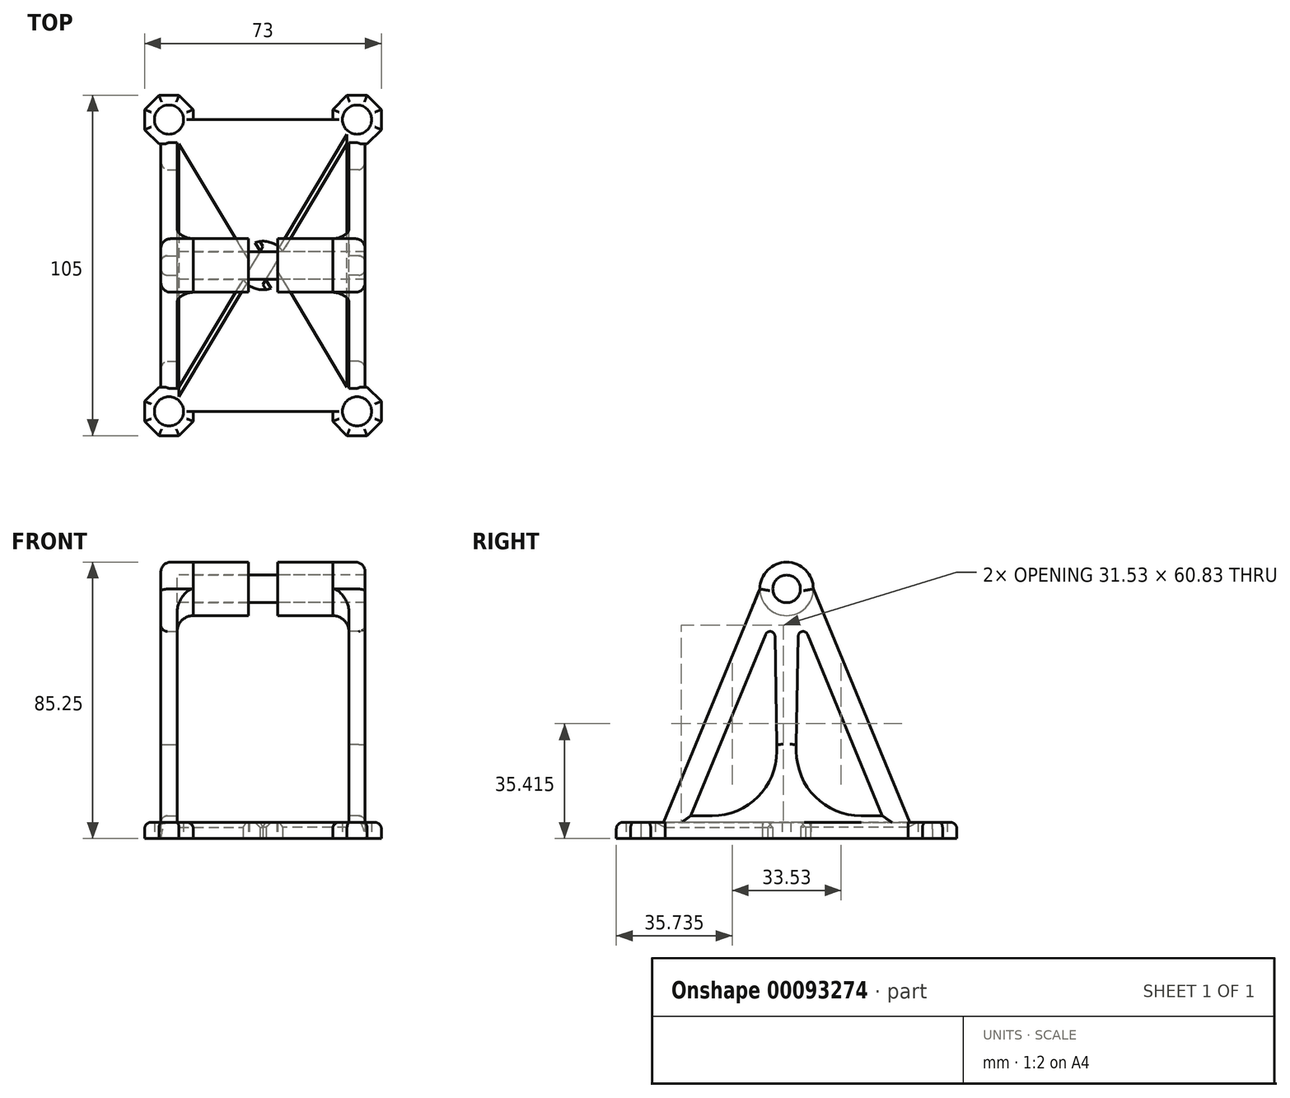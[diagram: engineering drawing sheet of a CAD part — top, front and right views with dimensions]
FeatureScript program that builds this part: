
annotation { "Feature Type Name" : "Feature", "Feature Type Description" : "" }
export const myFeature = defineFeature(function(context is Context, id is Id, definition is map)
    precondition{}
    {
        {
            assignVariable(context, id + "F0", {"name" : "shell", "anyValue" : 2.5});
        }
        {
            assignVariable(context, id + "F1", {"name" : "bucket_width", "anyValue" : 48});
        }
        {
            assignVariable(context, id + "F2", {"name" : "bearing_width", "anyValue" : 7});
        }
        {
            var Q0;
            Q0=qCreatedBy(makeId("Top.planeOp"),FACE);
            var sketch = newSketch(context, id + "F3", { "sketchPlane" : qUnion([Q0])});
            skLineSegment(sketch, "E0.bottom", {"start": v(29, -45) * mm, "end": v(-29, -45) * mm});
            skLineSegment(sketch, "E0.top", {"start": v(29, 45) * mm, "end": v(-29, 45) * mm});
            skLineSegment(sketch, "E0.left", {"start": v(29, -45) * mm, "end": v(29, 45) * mm});
            skLineSegment(sketch, "E0.right", {"start": v(-29, -45) * mm, "end": v(-29, 45) * mm});
            skPoint(sketch, "E0.middle", {"position": v(0, 0) * mm});
            skCircle(sketch, "E1.cCircle", {"center": v(-29, 45) * mm, "radius": 7.5 * mm, "construction": true});
            skLineSegment(sketch, "E1.0", {"start": v(-21.5, 48.1) * mm, "end": v(-21.5, 41.9) * mm});
            skLineSegment(sketch, "E1.1", {"start": v(-21.5, 41.9) * mm, "end": v(-25.9, 37.5) * mm});
            skLineSegment(sketch, "E1.2", {"start": v(-25.9, 37.5) * mm, "end": v(-32.1, 37.5) * mm});
            skLineSegment(sketch, "E1.3", {"start": v(-32.1, 37.5) * mm, "end": v(-36.5, 41.9) * mm});
            skLineSegment(sketch, "E1.4", {"start": v(-36.5, 41.9) * mm, "end": v(-36.5, 48.1) * mm});
            skLineSegment(sketch, "E1.5", {"start": v(-36.5, 48.1) * mm, "end": v(-32.1, 52.5) * mm});
            skLineSegment(sketch, "E1.6", {"start": v(-32.1, 52.5) * mm, "end": v(-25.9, 52.5) * mm});
            skLineSegment(sketch, "E1.7", {"start": v(-25.9, 52.5) * mm, "end": v(-21.5, 48.1) * mm});
            skPoint(sketch, "E1.0.midPoint", {"position": v(-21.5, 45) * mm});
            skCircle(sketch, "E2.cCircle", {"center": v(-29, -45) * mm, "radius": 7.5 * mm, "construction": true});
            skLineSegment(sketch, "E2.0", {"start": v(-32.1, -37.5) * mm, "end": v(-25.9, -37.5) * mm});
            skLineSegment(sketch, "E2.1", {"start": v(-25.9, -37.5) * mm, "end": v(-21.5, -41.9) * mm});
            skLineSegment(sketch, "E2.2", {"start": v(-21.5, -41.9) * mm, "end": v(-21.5, -48.1) * mm});
            skLineSegment(sketch, "E2.3", {"start": v(-21.5, -48.1) * mm, "end": v(-25.9, -52.5) * mm});
            skLineSegment(sketch, "E2.4", {"start": v(-25.9, -52.5) * mm, "end": v(-32.1, -52.5) * mm});
            skLineSegment(sketch, "E2.5", {"start": v(-32.1, -52.5) * mm, "end": v(-36.5, -48.1) * mm});
            skLineSegment(sketch, "E2.6", {"start": v(-36.5, -48.1) * mm, "end": v(-36.5, -41.9) * mm});
            skLineSegment(sketch, "E2.7", {"start": v(-36.5, -41.9) * mm, "end": v(-32.1, -37.5) * mm});
            skPoint(sketch, "E2.0.midPoint", {"position": v(-29, -37.5) * mm});
            skCircle(sketch, "E3.cCircle", {"center": v(29, -45) * mm, "radius": 7.5 * mm, "construction": true});
            skLineSegment(sketch, "E3.0", {"start": v(25.9, -37.5) * mm, "end": v(32.1, -37.5) * mm});
            skLineSegment(sketch, "E3.1", {"start": v(32.1, -37.5) * mm, "end": v(36.5, -41.9) * mm});
            skLineSegment(sketch, "E3.2", {"start": v(36.5, -41.9) * mm, "end": v(36.5, -48.1) * mm});
            skLineSegment(sketch, "E3.3", {"start": v(36.5, -48.1) * mm, "end": v(32.1, -52.5) * mm});
            skLineSegment(sketch, "E3.4", {"start": v(32.1, -52.5) * mm, "end": v(25.9, -52.5) * mm});
            skLineSegment(sketch, "E3.5", {"start": v(25.9, -52.5) * mm, "end": v(21.5, -48.1) * mm});
            skLineSegment(sketch, "E3.6", {"start": v(21.5, -48.1) * mm, "end": v(21.5, -41.9) * mm});
            skLineSegment(sketch, "E3.7", {"start": v(21.5, -41.9) * mm, "end": v(25.9, -37.5) * mm});
            skPoint(sketch, "E3.0.midPoint", {"position": v(29, -37.5) * mm});
            skCircle(sketch, "E4.cCircle", {"center": v(29, 45) * mm, "radius": 7.5 * mm, "construction": true});
            skLineSegment(sketch, "E4.0", {"start": v(32.1, 37.5) * mm, "end": v(25.9, 37.5) * mm});
            skLineSegment(sketch, "E4.1", {"start": v(25.9, 37.5) * mm, "end": v(21.5, 41.9) * mm});
            skLineSegment(sketch, "E4.2", {"start": v(21.5, 41.9) * mm, "end": v(21.5, 48.1) * mm});
            skLineSegment(sketch, "E4.3", {"start": v(21.5, 48.1) * mm, "end": v(25.9, 52.5) * mm});
            skLineSegment(sketch, "E4.4", {"start": v(25.9, 52.5) * mm, "end": v(32.1, 52.5) * mm});
            skLineSegment(sketch, "E4.5", {"start": v(32.1, 52.5) * mm, "end": v(36.5, 48.1) * mm});
            skLineSegment(sketch, "E4.6", {"start": v(36.5, 48.1) * mm, "end": v(36.5, 41.9) * mm});
            skLineSegment(sketch, "E4.7", {"start": v(36.5, 41.9) * mm, "end": v(32.1, 37.5) * mm});
            skPoint(sketch, "E4.0.midPoint", {"position": v(29, 37.5) * mm});
            skLineSegment(sketch, "E5", {"start": v(-25.9, 37.5) * mm, "end": v(21.5, -41.9) * mm});
            skLineSegment(sketch, "E6", {"start": v(25.9, -37.5) * mm, "end": v(-21.5, 41.9) * mm});
            skLineSegment(sketch, "E7", {"start": v(21.5, 41.9) * mm, "end": v(-25.9, -37.5) * mm});
            skLineSegment(sketch, "E8", {"start": v(-21.5, -41.9) * mm, "end": v(25.9, 37.5) * mm});
            skLineSegment(sketch, "E9", {"start": v(25.9, -37.5) * mm, "end": v(25.9, 37.5) * mm});
            skLineSegment(sketch, "E10", {"start": v(21.5, 41.9) * mm, "end": v(-21.5, 41.9) * mm});
            skLineSegment(sketch, "E11", {"start": v(-25.9, 37.5) * mm, "end": v(-25.9, -37.5) * mm});
            skLineSegment(sketch, "E12", {"start": v(-21.5, -41.9) * mm, "end": v(21.5, -41.9) * mm});
            skCircle(sketch, "E13", {"center": v(0, 0) * mm, "radius": 7.5 * mm});
            skCircle(sketch, "E14", {"center": v(0, 0) * mm, "radius": 4.5 * mm});
            skCircle(sketch, "E15", {"center": v(-29, 45) * mm, "radius": 4.5 * mm});
            skCircle(sketch, "E16", {"center": v(29, 45) * mm, "radius": 4.5 * mm});
            skCircle(sketch, "E17", {"center": v(29, -45) * mm, "radius": 4.5 * mm});
            skCircle(sketch, "E18", {"center": v(-29, -45) * mm, "radius": 4.5 * mm});
            skLineSegment(sketch, "E19", {"start": v(0, 0) * mm, "end": v(24, 0) * mm, "construction": true});
            skPoint(sketch, "E19.endSnap0", {"position": v(25.9, 0) * mm});
            skSolve(sketch);
        }
        {
            var Q0;
            Q0=qCreatedBy(makeId("Right.planeOp"),FACE);
            var sketch = newSketch(context, id + "F4", { "sketchPlane" : qUnion([Q0])});
            skLineSegment(sketch, "E20", {"start": v(0, 0) * mm, "end": v(0, 77) * mm, "construction": true});
            skCircle(sketch, "E21", {"center": v(0, 77) * mm, "radius": 4.25 * mm});
            skCircle(sketch, "E22.0", {"center": v(0, 77) * mm, "radius": 8.25 * mm});
            skLineSegment(sketch, "E23", {"start": v(0, 0) * mm, "end": v(40, 0) * mm});
            skLineSegment(sketch, "E24", {"start": v(0, 0) * mm, "end": v(-40, 0) * mm});
            skLineSegment(sketch, "E25", {"start": v(8.25, 77) * mm, "end": v(-8.25, 77) * mm, "construction": true});
            skLineSegment(sketch, "E26", {"start": v(8.25, 77) * mm, "end": v(40, 0) * mm});
            skLineSegment(sketch, "E27", {"start": v(-8.25, 77) * mm, "end": v(-40, 0) * mm});
            skLineSegment(sketch, "E28.0", {"start": v(3.72, 69.63) * mm, "end": v(29.54, 7) * mm});
            skLineSegment(sketch, "E28.1", {"start": v(0, 7) * mm, "end": v(29.54, 7) * mm});
            skLineSegment(sketch, "E28.2", {"start": v(0, 7) * mm, "end": v(-29.54, 7) * mm});
            skLineSegment(sketch, "E28.3", {"start": v(-3.72, 69.63) * mm, "end": v(-29.54, 7) * mm});
            skLineSegment(sketch, "E29", {"start": v(-3, 8.14) * mm, "end": v(0, 8.14) * mm, "construction": true});
            skLineSegment(sketch, "E30", {"start": v(0, 8.14) * mm, "end": v(3, 8.14) * mm, "construction": true});
            skLineSegment(sketch, "E31", {"start": v(3, 7) * mm, "end": v(3, 29.03) * mm});
            skLineSegment(sketch, "E32", {"start": v(-3, 7) * mm, "end": v(-3, 29.03) * mm});
            skLineSegment(sketch, "E33", {"start": v(3.72, 69.63) * mm, "end": v(3, 29.03) * mm});
            skLineSegment(sketch, "E34", {"start": v(-3.72, 69.63) * mm, "end": v(-3, 29.03) * mm});
            skSolve(sketch);
        }
        {
            var Q0;
            {var subQ0=sQuery(id+"F3.wireOp",EDGE,"E2.3");Q0=makeQuery(id+"F3.imprint","IMPRINT",FACE,{"disambiguationData":[TD([[makeQuery(id+"F3.imprint","IMPRINT",EDGE,{"derivedFrom":subQ0}),-1.0]])]});}
            var Q1;
            {var subQ0=sQuery(id+"F3.wireOp",EDGE,"E2.1");Q1=makeQuery(id+"F3.imprint","IMPRINT",FACE,{"disambiguationData":[TD([[makeQuery(id+"F3.imprint","IMPRINT",EDGE,{"derivedFrom":subQ0}),-1.0]])]});}
            var Q2;
            {var subQ5=sQuery(id+"F3.wireOp",EDGE,"E11");Q2=makeQuery(id+"F3.imprint","IMPRINT",FACE,{"disambiguationData":[TD([[makeQuery(id+"F3.imprint","IMPRINT",EDGE,{"derivedFrom":subQ5}),-1.0]])]});}
            var Q3;
            {var subQ9=sQuery(id+"F3.wireOp",EDGE,"E1.3");Q3=makeQuery(id+"F3.imprint","IMPRINT",FACE,{"disambiguationData":[TD([[makeQuery(id+"F3.imprint","IMPRINT",EDGE,{"derivedFrom":subQ9}),-1.0]])]});}
            var Q4;
            {var subQ0=sQuery(id+"F3.wireOp",EDGE,"E1.1");Q4=makeQuery(id+"F3.imprint","IMPRINT",FACE,{"disambiguationData":[TD([[makeQuery(id+"F3.imprint","IMPRINT",EDGE,{"derivedFrom":subQ0}),-1.0]])]});}
            var Q5;
            {var subQ5=sQuery(id+"F3.wireOp",EDGE,"E1.1");Q5=makeQuery(id+"F3.imprint","IMPRINT",FACE,{"disambiguationData":[TD([[makeQuery(id+"F3.imprint","IMPRINT",EDGE,{"derivedFrom":subQ5}),1.0]])]});}
            var Q6;
            {var subQ5=sQuery(id+"F3.wireOp",EDGE,"E10");Q6=makeQuery(id+"F3.imprint","IMPRINT",FACE,{"disambiguationData":[TD([[makeQuery(id+"F3.imprint","IMPRINT",EDGE,{"derivedFrom":subQ5}),-1.0]])]});}
            var Q7;
            {var subQ0=sQuery(id+"F3.wireOp",EDGE,"E4.3");Q7=makeQuery(id+"F3.imprint","IMPRINT",FACE,{"disambiguationData":[TD([[makeQuery(id+"F3.imprint","IMPRINT",EDGE,{"derivedFrom":subQ0}),-1.0]])]});}
            var Q8;
            {var subQ1=sQuery(id+"F3.wireOp",EDGE,"E4.1");Q8=makeQuery(id+"F3.imprint","IMPRINT",FACE,{"disambiguationData":[TD([[makeQuery(id+"F3.imprint","IMPRINT",EDGE,{"derivedFrom":subQ1}),1.0]])]});}
            var Q9;
            {var subQ0=sQuery(id+"F3.wireOp",EDGE,"E13");var subQ1=sQuery(id+"F3.wireOp",EDGE,"E5");var subQ2=makeQuery(id+"F3.imprint","INTERSECT",VERTEX,{"disambiguationData":[OD(0.0)],"derivedFrom":[subQ1,subQ0]});Q9=makeQuery(id+"F3.imprint","IMPRINT",FACE,{"disambiguationData":[TD([[makeQuery(id+"F3.imprint","IMPRINT",EDGE,{"disambiguationData":[TD([[subQ2,-1.0]])],"derivedFrom":subQ1}),1.0]])]});}
            var Q10;
            {var subQ0=sQuery(id+"F3.wireOp",EDGE,"E13");var subQ1=sQuery(id+"F3.wireOp",EDGE,"E5");var subQ2=makeQuery(id+"F3.imprint","INTERSECT",VERTEX,{"disambiguationData":[OD(0.0)],"derivedFrom":[subQ1,subQ0]});Q10=makeQuery(id+"F3.imprint","IMPRINT",FACE,{"disambiguationData":[TD([[makeQuery(id+"F3.imprint","IMPRINT",EDGE,{"disambiguationData":[TD([[subQ2,-1.0]])],"derivedFrom":subQ1}),-1.0]])]});}
            var Q11;
            {var subQ0=sQuery(id+"F3.wireOp",EDGE,"E13");var subQ1=sQuery(id+"F3.wireOp",EDGE,"E6");var subQ2=makeQuery(id+"F3.imprint","INTERSECT",VERTEX,{"disambiguationData":[OD(0.0)],"derivedFrom":[subQ1,subQ0]});Q11=makeQuery(id+"F3.imprint","IMPRINT",FACE,{"disambiguationData":[TD([[makeQuery(id+"F3.imprint","IMPRINT",EDGE,{"disambiguationData":[TD([[subQ2,-1.0]])],"derivedFrom":subQ1}),-1.0]])]});}
            var Q12;
            {var subQ6=sQuery(id+"F3.wireOp",EDGE,"E3.7");Q12=makeQuery(id+"F3.imprint","IMPRINT",FACE,{"disambiguationData":[TD([[makeQuery(id+"F3.imprint","IMPRINT",EDGE,{"derivedFrom":subQ6}),1.0]])]});}
            var Q13;
            {var subQ1=sQuery(id+"F3.wireOp",EDGE,"E2.1");Q13=makeQuery(id+"F3.imprint","IMPRINT",FACE,{"disambiguationData":[TD([[makeQuery(id+"F3.imprint","IMPRINT",EDGE,{"derivedFrom":subQ1}),1.0]])]});}
            var Q14;
            {var subQ5=sQuery(id+"F3.wireOp",EDGE,"E12");Q14=makeQuery(id+"F3.imprint","IMPRINT",FACE,{"disambiguationData":[TD([[makeQuery(id+"F3.imprint","IMPRINT",EDGE,{"derivedFrom":subQ5}),-1.0]])]});}
            var Q15;
            {var subQ0=sQuery(id+"F3.wireOp",EDGE,"E3.7");Q15=makeQuery(id+"F3.imprint","IMPRINT",FACE,{"disambiguationData":[TD([[makeQuery(id+"F3.imprint","IMPRINT",EDGE,{"derivedFrom":subQ0}),-1.0]])]});}
            var Q16;
            {var subQ5=sQuery(id+"F3.wireOp",EDGE,"E9");Q16=makeQuery(id+"F3.imprint","IMPRINT",FACE,{"disambiguationData":[TD([[makeQuery(id+"F3.imprint","IMPRINT",EDGE,{"derivedFrom":subQ5}),-1.0]])]});}
            var Q17;
            {var subQ0=sQuery(id+"F3.wireOp",EDGE,"E3.1");Q17=makeQuery(id+"F3.imprint","IMPRINT",FACE,{"disambiguationData":[TD([[makeQuery(id+"F3.imprint","IMPRINT",EDGE,{"derivedFrom":subQ0}),-1.0]])]});}
            var Q18;
            {var subQ9=sQuery(id+"F3.wireOp",EDGE,"E4.1");Q18=makeQuery(id+"F3.imprint","IMPRINT",FACE,{"disambiguationData":[TD([[makeQuery(id+"F3.imprint","IMPRINT",EDGE,{"derivedFrom":subQ9}),-1.0]])]});}
            var Q19;
            {var subQ0=sQuery(id+"F3.wireOp",EDGE,"E14");var subQ1=sQuery(id+"F3.wireOp",EDGE,"E5");var subQ2=makeQuery(id+"F3.imprint","INTERSECT",VERTEX,{"disambiguationData":[OD(1.0)],"derivedFrom":[subQ1,subQ0]});Q19=makeQuery(id+"F3.imprint","IMPRINT",FACE,{"disambiguationData":[TD([[makeQuery(id+"F3.imprint","IMPRINT",EDGE,{"disambiguationData":[TD([[subQ2,-1.0]])],"derivedFrom":subQ1}),-1.0]])]});}
            var Q20;
            {var subQ0=sQuery(id+"F3.wireOp",EDGE,"E14");var subQ1=sQuery(id+"F3.wireOp",EDGE,"E5");var subQ2=makeQuery(id+"F3.imprint","INTERSECT",VERTEX,{"disambiguationData":[OD(1.0)],"derivedFrom":[subQ1,subQ0]});Q20=makeQuery(id+"F3.imprint","IMPRINT",FACE,{"disambiguationData":[TD([[makeQuery(id+"F3.imprint","IMPRINT",EDGE,{"disambiguationData":[TD([[subQ2,-1.0]])],"derivedFrom":subQ1}),1.0]])]});}
            var Q21;
            {var subQ0=sQuery(id+"F3.wireOp",EDGE,"E14");var subQ1=sQuery(id+"F3.wireOp",EDGE,"E6");var subQ2=makeQuery(id+"F3.imprint","INTERSECT",VERTEX,{"disambiguationData":[OD(1.0)],"derivedFrom":[subQ1,subQ0]});Q21=makeQuery(id+"F3.imprint","IMPRINT",FACE,{"disambiguationData":[TD([[makeQuery(id+"F3.imprint","IMPRINT",EDGE,{"disambiguationData":[TD([[subQ2,-1.0]])],"derivedFrom":subQ1}),-1.0]])]});}
            var Q22;
            {var subQ0=sQuery(id+"F3.wireOp",EDGE,"E14");var subQ1=sQuery(id+"F3.wireOp",EDGE,"E6");var subQ2=makeQuery(id+"F3.imprint","INTERSECT",VERTEX,{"disambiguationData":[OD(1.0)],"derivedFrom":[subQ1,subQ0]});Q22=makeQuery(id+"F3.imprint","IMPRINT",FACE,{"disambiguationData":[TD([[makeQuery(id+"F3.imprint","IMPRINT",EDGE,{"disambiguationData":[TD([[subQ2,-1.0]])],"derivedFrom":subQ1}),1.0]])]});}
            var Q23;
            {var subQ0=sQuery(id+"F3.wireOp",EDGE,"E13");var subQ1=sQuery(id+"F3.wireOp",EDGE,"E6");var subQ2=makeQuery(id+"F3.imprint","INTERSECT",VERTEX,{"disambiguationData":[OD(0.0)],"derivedFrom":[subQ1,subQ0]});Q23=makeQuery(id+"F3.imprint","IMPRINT",FACE,{"disambiguationData":[TD([[makeQuery(id+"F3.imprint","IMPRINT",EDGE,{"disambiguationData":[TD([[subQ2,-1.0]])],"derivedFrom":subQ1}),1.0]])]});}
            var Q24;
            {var subQ0=sQuery(id+"F3.wireOp",EDGE,"E13");var subQ1=sQuery(id+"F3.wireOp",EDGE,"E5");var subQ2=makeQuery(id+"F3.imprint","INTERSECT",VERTEX,{"disambiguationData":[OD(1.0)],"derivedFrom":[subQ1,subQ0]});Q24=makeQuery(id+"F3.imprint","IMPRINT",FACE,{"disambiguationData":[TD([[makeQuery(id+"F3.imprint","IMPRINT",EDGE,{"disambiguationData":[TD([[subQ2,-1.0]])],"derivedFrom":subQ1}),1.0]])]});}
            var Q25;
            {var subQ0=sQuery(id+"F3.wireOp",EDGE,"E13");var subQ1=sQuery(id+"F3.wireOp",EDGE,"E6");var subQ2=makeQuery(id+"F3.imprint","INTERSECT",VERTEX,{"disambiguationData":[OD(1.0)],"derivedFrom":[subQ1,subQ0]});Q25=makeQuery(id+"F3.imprint","IMPRINT",FACE,{"disambiguationData":[TD([[makeQuery(id+"F3.imprint","IMPRINT",EDGE,{"disambiguationData":[TD([[subQ2,-1.0]])],"derivedFrom":subQ1}),1.0]])]});}
            extrude(context, id + "F5", {"entities" : qUnion([Q0, Q1, Q2, Q3, Q4, Q5, Q6, Q7, Q8, Q9, Q10, Q11, Q12, Q13, Q14, Q15, Q16, Q17, Q18, Q19, Q20, Q21, Q22, Q23, Q24, Q25]), "depth" : 5 * mm});
        }
        {
            var Q0;
            {var subQ5=sQuery(id+"F4.wireOp",EDGE,"E27");Q0=makeQuery(id+"F4.imprint","IMPRINT",FACE,{"disambiguationData":[TD([[makeQuery(id+"F4.imprint","IMPRINT",EDGE,{"derivedFrom":subQ5}),1.0]])]});}
            var Q1;
            {var subQ4=sQuery(id+"F4.wireOp",EDGE,"E26");Q1=makeQuery(id+"F4.imprint","IMPRINT",FACE,{"disambiguationData":[TD([[makeQuery(id+"F4.imprint","IMPRINT",EDGE,{"derivedFrom":subQ4}),-1.0]])]});}
            var Q2;
            {var subQ7=sQuery(id+"F4.wireOp",EDGE,"E24");var subQ8=sQuery(id+"F4.wireOp",EDGE,"E23");var subQ9=makeQuery(id+"F4.imprint","INTERSECT",VERTEX,{"derivedFrom":[subQ8,subQ7]});Q2=makeQuery(id+"F4.imprint","IMPRINT",FACE,{"disambiguationData":[TD([[makeQuery(id+"F4.imprint","IMPRINT",EDGE,{"disambiguationData":[TD([[subQ9,-1.0]])],"derivedFrom":subQ8}),1.0]])]});}
            var Q3;
            Q3=makeQuery(id+"F4.imprint","IMPRINT",FACE,{"disambiguationData":[TD([[makeQuery(id+"F4.imprint","IMPRINT",EDGE,{"derivedFrom":sQuery(id+"F4.wireOp",EDGE,"E21")}),-1.0]])]});
            var Q4;
            Q4=makeQuery(id+"F4.imprint","IMPRINT",FACE,{"disambiguationData":[TD([[makeQuery(id+"F4.imprint","IMPRINT",EDGE,{"derivedFrom":sQuery(id+"F4.wireOp",EDGE,"E21")}),-1.0]])]});
            var Q5;
            {var subQ5=sQuery(id+"F4.wireOp",EDGE,"E27");Q5=makeQuery(id+"F4.imprint","IMPRINT",FACE,{"disambiguationData":[TD([[makeQuery(id+"F4.imprint","IMPRINT",EDGE,{"derivedFrom":subQ5}),1.0]])]});}
            var Q6;
            Q6=makeQuery(id+"F4.imprint","IMPRINT",FACE,{"disambiguationData":[TD([[makeQuery(id+"F4.imprint","IMPRINT",EDGE,{"derivedFrom":sQuery(id+"F4.wireOp",EDGE,"908c2eed-a312-402c-85c4-66b7b7d972e5.4")}),1.0]])]});
            var Q7;
            {var subQ3=sQuery(id+"F4.wireOp",EDGE,"3dacc5b1-dc25-4eaf-9f2e-9f7119090daa.0");var subQ5=sQuery(id+"F4.wireOp",EDGE,"908c2eed-a312-402c-85c4-66b7b7d972e5.0");var subQ6=makeQuery(id+"F4.imprint","INTERSECT",VERTEX,{"derivedFrom":[subQ3,subQ5]});Q7=makeQuery(id+"F4.imprint","IMPRINT",FACE,{"disambiguationData":[TD([[makeQuery(id+"F4.imprint","IMPRINT",EDGE,{"disambiguationData":[TD([[subQ6,1.0]])],"derivedFrom":subQ3}),1.0]])]});}
            var Q8;
            Q8=makeQuery(id+"F4.imprint","IMPRINT",FACE,{"disambiguationData":[TD([[makeQuery(id+"F4.imprint","IMPRINT",EDGE,{"derivedFrom":sQuery(id+"F4.wireOp",EDGE,"908c2eed-a312-402c-85c4-66b7b7d972e5.1")}),1.0]])]});
            var Q9;
            {var subQ1=sQuery(id+"F4.wireOp",EDGE,"E28.2");var subQ6=sQuery(id+"F4.wireOp",EDGE,"E28.1");var subQ10=makeQuery(id+"F4.imprint","INTERSECT",VERTEX,{"derivedFrom":[subQ6,subQ1]});Q9=makeQuery(id+"F4.imprint","IMPRINT",FACE,{"disambiguationData":[TD([[makeQuery(id+"F4.imprint","IMPRINT",EDGE,{"disambiguationData":[TD([[subQ10,-1.0]])],"derivedFrom":subQ6}),1.0]])]});}
            var Q10;
            {var subQ4=sQuery(id+"F4.wireOp",EDGE,"E26");Q10=makeQuery(id+"F4.imprint","IMPRINT",FACE,{"disambiguationData":[TD([[makeQuery(id+"F4.imprint","IMPRINT",EDGE,{"derivedFrom":subQ4}),-1.0]])]});}
            var Q11;
            {var subQ0=sQuery(id+"F4.wireOp",EDGE,"908c2eed-a312-402c-85c4-66b7b7d972e5.1");Q11=makeQuery(id+"F4.imprint","IMPRINT",FACE,{"disambiguationData":[TD([[makeQuery(id+"F4.imprint","IMPRINT",EDGE,{"derivedFrom":subQ0}),-1.0]])]});}
            var Q12;
            {var subQ1=sQuery(id+"F4.wireOp",EDGE,"908c2eed-a312-402c-85c4-66b7b7d972e5.2");var subQ3=sQuery(id+"F4.wireOp",EDGE,"3dacc5b1-dc25-4eaf-9f2e-9f7119090daa.0");var subQ4=makeQuery(id+"F4.imprint","INTERSECT",VERTEX,{"derivedFrom":[subQ3,subQ1]});Q12=makeQuery(id+"F4.imprint","IMPRINT",FACE,{"disambiguationData":[TD([[makeQuery(id+"F4.imprint","IMPRINT",EDGE,{"disambiguationData":[TD([[subQ4,-1.0]])],"derivedFrom":subQ3}),1.0]])]});}
            var Q13;
            {var subQ0=sQuery(id+"F4.wireOp",EDGE,"908c2eed-a312-402c-85c4-66b7b7d972e5.4");Q13=makeQuery(id+"F4.imprint","IMPRINT",FACE,{"disambiguationData":[TD([[makeQuery(id+"F4.imprint","IMPRINT",EDGE,{"derivedFrom":subQ0}),-1.0]])]});}
            extrude(context, id + "F6", {"entities" : qUnion([Q0, Q1, Q2, Q3, Q4, Q5, Q6, Q7, Q8, Q9, Q10, Q11, Q12, Q13]), "operationType" : NewBodyOperationType.ADD, "depth" : (getVariable(context, 'bucket_width') / 2 + getVariable(context, 'shell') * 3) * mm, "hasSecondDirection" : true, "secondDirectionOppositeDirection" : false, "secondDirectionDepth" : (getVariable(context, 'bucket_width') / 2 + getVariable(context, 'shell')) * mm});
        }
        {
            var Q0;
            {var subQ5=sQuery(id+"F4.wireOp",EDGE,"E27");Q0=makeQuery(id+"F4.imprint","IMPRINT",FACE,{"disambiguationData":[TD([[makeQuery(id+"F4.imprint","IMPRINT",EDGE,{"derivedFrom":subQ5}),1.0]])]});}
            var Q1;
            {var subQ4=sQuery(id+"F4.wireOp",EDGE,"E26");Q1=makeQuery(id+"F4.imprint","IMPRINT",FACE,{"disambiguationData":[TD([[makeQuery(id+"F4.imprint","IMPRINT",EDGE,{"derivedFrom":subQ4}),-1.0]])]});}
            var Q2;
            {var subQ7=sQuery(id+"F4.wireOp",EDGE,"E24");var subQ8=sQuery(id+"F4.wireOp",EDGE,"E23");var subQ9=makeQuery(id+"F4.imprint","INTERSECT",VERTEX,{"derivedFrom":[subQ8,subQ7]});Q2=makeQuery(id+"F4.imprint","IMPRINT",FACE,{"disambiguationData":[TD([[makeQuery(id+"F4.imprint","IMPRINT",EDGE,{"disambiguationData":[TD([[subQ9,-1.0]])],"derivedFrom":subQ8}),1.0]])]});}
            var Q3;
            Q3=makeQuery(id+"F4.imprint","IMPRINT",FACE,{"disambiguationData":[TD([[makeQuery(id+"F4.imprint","IMPRINT",EDGE,{"derivedFrom":sQuery(id+"F4.wireOp",EDGE,"E21")}),-1.0]])]});
            var Q4;
            Q4=makeQuery(id+"F4.imprint","IMPRINT",FACE,{"disambiguationData":[TD([[makeQuery(id+"F4.imprint","IMPRINT",EDGE,{"derivedFrom":sQuery(id+"F4.wireOp",EDGE,"E21")}),1.0]])]});
            var Q5;
            Q5=makeQuery(id+"F4.imprint","IMPRINT",FACE,{"disambiguationData":[TD([[makeQuery(id+"F4.imprint","IMPRINT",EDGE,{"derivedFrom":sQuery(id+"F4.wireOp",EDGE,"E21")}),-1.0]])]});
            var Q6;
            Q6=makeQuery(id+"F4.imprint","IMPRINT",FACE,{"disambiguationData":[TD([[makeQuery(id+"F4.imprint","IMPRINT",EDGE,{"derivedFrom":sQuery(id+"F4.wireOp",EDGE,"E21")}),-1.0]])]});
            var Q7;
            Q7=makeQuery(id+"F4.imprint","IMPRINT",FACE,{"disambiguationData":[TD([[makeQuery(id+"F4.imprint","IMPRINT",EDGE,{"derivedFrom":sQuery(id+"F4.wireOp",EDGE,"E21")}),-1.0]])]});
            var Q8;
            {var subQ5=sQuery(id+"F4.wireOp",EDGE,"E27");Q8=makeQuery(id+"F4.imprint","IMPRINT",FACE,{"disambiguationData":[TD([[makeQuery(id+"F4.imprint","IMPRINT",EDGE,{"derivedFrom":subQ5}),1.0]])]});}
            var Q9;
            {var subQ4=sQuery(id+"F4.wireOp",EDGE,"E26");Q9=makeQuery(id+"F4.imprint","IMPRINT",FACE,{"disambiguationData":[TD([[makeQuery(id+"F4.imprint","IMPRINT",EDGE,{"derivedFrom":subQ4}),-1.0]])]});}
            var Q10;
            Q10=makeQuery(id+"F4.imprint","IMPRINT",FACE,{"disambiguationData":[TD([[makeQuery(id+"F4.imprint","IMPRINT",EDGE,{"derivedFrom":sQuery(id+"F4.wireOp",EDGE,"908c2eed-a312-402c-85c4-66b7b7d972e5.1")}),1.0]])]});
            var Q11;
            {var subQ5=sQuery(id+"F4.wireOp",EDGE,"908c2eed-a312-402c-85c4-66b7b7d972e5.1");Q11=makeQuery(id+"F4.imprint","IMPRINT",FACE,{"disambiguationData":[TD([[makeQuery(id+"F4.imprint","IMPRINT",EDGE,{"derivedFrom":subQ5}),-1.0]])]});}
            var Q12;
            {var subQ3=sQuery(id+"F4.wireOp",EDGE,"3dacc5b1-dc25-4eaf-9f2e-9f7119090daa.0");var subQ5=sQuery(id+"F4.wireOp",EDGE,"908c2eed-a312-402c-85c4-66b7b7d972e5.0");var subQ6=makeQuery(id+"F4.imprint","INTERSECT",VERTEX,{"derivedFrom":[subQ3,subQ5]});Q12=makeQuery(id+"F4.imprint","IMPRINT",FACE,{"disambiguationData":[TD([[makeQuery(id+"F4.imprint","IMPRINT",EDGE,{"disambiguationData":[TD([[subQ6,1.0]])],"derivedFrom":subQ3}),1.0]])]});}
            var Q13;
            {var subQ5=sQuery(id+"F4.wireOp",EDGE,"908c2eed-a312-402c-85c4-66b7b7d972e5.4");Q13=makeQuery(id+"F4.imprint","IMPRINT",FACE,{"disambiguationData":[TD([[makeQuery(id+"F4.imprint","IMPRINT",EDGE,{"derivedFrom":subQ5}),-1.0]])]});}
            var Q14;
            Q14=makeQuery(id+"F4.imprint","IMPRINT",FACE,{"disambiguationData":[TD([[makeQuery(id+"F4.imprint","IMPRINT",EDGE,{"derivedFrom":sQuery(id+"F4.wireOp",EDGE,"908c2eed-a312-402c-85c4-66b7b7d972e5.4")}),1.0]])]});
            var Q15;
            {var subQ1=sQuery(id+"F4.wireOp",EDGE,"E28.2");var subQ6=sQuery(id+"F4.wireOp",EDGE,"E28.1");var subQ10=makeQuery(id+"F4.imprint","INTERSECT",VERTEX,{"derivedFrom":[subQ6,subQ1]});Q15=makeQuery(id+"F4.imprint","IMPRINT",FACE,{"disambiguationData":[TD([[makeQuery(id+"F4.imprint","IMPRINT",EDGE,{"disambiguationData":[TD([[subQ10,-1.0]])],"derivedFrom":subQ6}),1.0]])]});}
            var Q16;
            {var subQ1=sQuery(id+"F4.wireOp",EDGE,"908c2eed-a312-402c-85c4-66b7b7d972e5.2");var subQ3=sQuery(id+"F4.wireOp",EDGE,"3dacc5b1-dc25-4eaf-9f2e-9f7119090daa.0");var subQ4=makeQuery(id+"F4.imprint","INTERSECT",VERTEX,{"derivedFrom":[subQ3,subQ1]});Q16=makeQuery(id+"F4.imprint","IMPRINT",FACE,{"disambiguationData":[TD([[makeQuery(id+"F4.imprint","IMPRINT",EDGE,{"disambiguationData":[TD([[subQ4,-1.0]])],"derivedFrom":subQ3}),1.0]])]});}
            extrude(context, id + "F7", {"entities" : qUnion([Q0, Q1, Q2, Q3, Q4, Q5, Q6, Q7, Q8, Q9, Q10, Q11, Q12, Q13, Q14, Q15, Q16]), "operationType" : NewBodyOperationType.ADD, "oppositeDirection" : true, "depth" : (getVariable(context, 'bucket_width') / 2 + getVariable(context, 'shell') * 3) * mm, "hasSecondDirection" : true, "secondDirectionOppositeDirection" : true, "secondDirectionDepth" : (getVariable(context, 'bucket_width') / 2 + getVariable(context, 'shell')) * mm});
        }
        {
            var Q0;
            Q0=makeQuery(id+"F4.imprint","IMPRINT",FACE,{"disambiguationData":[TD([[makeQuery(id+"F4.imprint","IMPRINT",EDGE,{"derivedFrom":sQuery(id+"F4.wireOp",EDGE,"E21")}),-1.0]])]});
            var Q1;
            {var subQ2=sQuery(id+"F4.wireOp",EDGE,"E28.0");var subQ7=sQuery(id+"F4.wireOp",EDGE,"E21");var subQ9=makeQuery(id+"F4.imprint","INTERSECT",VERTEX,{"derivedFrom":[subQ7,subQ2]});Q1=makeQuery(id+"F4.imprint","IMPRINT",FACE,{"disambiguationData":[TD([[makeQuery(id+"F4.imprint","IMPRINT",EDGE,{"disambiguationData":[TD([[subQ9,-1.0]])],"derivedFrom":subQ7}),-1.0]])]});}
            extrude(context, id + "F8", {"entities" : qUnion([Q0, Q1]), "operationType" : NewBodyOperationType.ADD, "depth" : (getVariable(context, 'bucket_width') / 2 + 7) * mm, "hasSecondDirection" : true, "secondDirectionOppositeDirection" : false, "secondDirectionDepth" : (getVariable(context, 'bucket_width') / 2 - getVariable(context, 'shell')) * mm});
        }
        {
            var Q0;
            {var subQ2=sQuery(id+"F4.wireOp",EDGE,"E28.3");var subQ7=sQuery(id+"F4.wireOp",EDGE,"E21");var subQ9=makeQuery(id+"F4.imprint","INTERSECT",VERTEX,{"derivedFrom":[subQ7,subQ2]});Q0=makeQuery(id+"F4.imprint","IMPRINT",FACE,{"disambiguationData":[TD([[makeQuery(id+"F4.imprint","IMPRINT",EDGE,{"disambiguationData":[TD([[subQ9,1.0]])],"derivedFrom":subQ7}),-1.0]])]});}
            var Q1;
            {var subQ0=sQuery(id+"F4.wireOp",EDGE,"dfa7258b-916b-41aa-b35c-9c5d3d2d38c0.0");var subQ1=sQuery(id+"F4.wireOp",EDGE,"E21");var subQ2=makeQuery(id+"F4.imprint","INTERSECT",VERTEX,{"derivedFrom":[subQ1,subQ0]});Q1=makeQuery(id+"F4.imprint","IMPRINT",FACE,{"disambiguationData":[TD([[makeQuery(id+"F4.imprint","IMPRINT",EDGE,{"disambiguationData":[TD([[subQ2,-1.0]])],"derivedFrom":subQ1}),-1.0]])]});}
            var Q2;
            {var subQ0=sQuery(id+"F4.wireOp",EDGE,"3dacc5b1-dc25-4eaf-9f2e-9f7119090daa.0");var subQ1=sQuery(id+"F4.wireOp",EDGE,"E21");var subQ2=makeQuery(id+"F4.imprint","INTERSECT",VERTEX,{"derivedFrom":[subQ1,subQ0]});Q2=makeQuery(id+"F4.imprint","IMPRINT",FACE,{"disambiguationData":[TD([[makeQuery(id+"F4.imprint","IMPRINT",EDGE,{"disambiguationData":[TD([[subQ2,-1.0]])],"derivedFrom":subQ1}),-1.0]])]});}
            var Q3;
            {var subQ0=sQuery(id+"F4.wireOp",EDGE,"dfa7258b-916b-41aa-b35c-9c5d3d2d38c0.0");var subQ1=sQuery(id+"F4.wireOp",EDGE,"E21");var subQ2=makeQuery(id+"F4.imprint","INTERSECT",VERTEX,{"derivedFrom":[subQ1,subQ0]});Q3=makeQuery(id+"F4.imprint","IMPRINT",FACE,{"disambiguationData":[TD([[makeQuery(id+"F4.imprint","IMPRINT",EDGE,{"disambiguationData":[TD([[subQ2,1.0]])],"derivedFrom":subQ1}),-1.0]])]});}
            var Q4;
            {var subQ0=sQuery(id+"F4.wireOp",EDGE,"E21");var subQ1=makeQuery(id+"F4.imprint","INTERSECT",VERTEX,{"derivedFrom":[subQ0,sQuery(id+"F4.wireOp",EDGE,"dfa7258b-916b-41aa-b35c-9c5d3d2d38c0.0")]});Q4=makeQuery(id+"F4.imprint","IMPRINT",FACE,{"disambiguationData":[TD([[makeQuery(id+"F4.imprint","IMPRINT",EDGE,{"disambiguationData":[TD([[subQ1,1.0]])],"derivedFrom":subQ0}),1.0]])]});}
            extrude(context, id + "F9", {"entities" : qUnion([Q0, Q1, Q2, Q3, Q4]), "operationType" : NewBodyOperationType.ADD, "oppositeDirection" : true, "depth" : (getVariable(context, 'bucket_width') / 2 + 7) * mm, "hasSecondDirection" : true, "secondDirectionOppositeDirection" : true, "secondDirectionDepth" : ((getVariable(context, 'bucket_width') / 2) - getVariable(context, 'shell')) * mm});
        }
        {
            var Q0;
            {var subQ0=sQuery(id+"F3.wireOp",EDGE,"E0.right");var subQ1=sQuery(id+"F3.wireOp",EDGE,"E0.bottom");var subQ2=makeQuery(id+"F3.imprint","INTERSECT",VERTEX,{"derivedFrom":[subQ1,subQ0]});Q0=makeQuery(id+"F3.imprint","IMPRINT",FACE,{"disambiguationData":[TD([[makeQuery(id+"F3.imprint","IMPRINT",EDGE,{"disambiguationData":[TD([[subQ2,1.0]])],"derivedFrom":subQ1}),-1.0]])]});}
            var Q1;
            {var subQ0=sQuery(id+"F3.wireOp",EDGE,"E0.right");var subQ1=sQuery(id+"F3.wireOp",EDGE,"E0.bottom");var subQ2=makeQuery(id+"F3.imprint","INTERSECT",VERTEX,{"derivedFrom":[subQ1,subQ0]});Q1=makeQuery(id+"F3.imprint","IMPRINT",FACE,{"disambiguationData":[TD([[makeQuery(id+"F3.imprint","IMPRINT",EDGE,{"disambiguationData":[TD([[subQ2,1.0]])],"derivedFrom":subQ1}),1.0]])]});}
            var Q2;
            {var subQ0=sQuery(id+"F3.wireOp",EDGE,"E0.left");var subQ1=sQuery(id+"F3.wireOp",EDGE,"E0.bottom");var subQ2=makeQuery(id+"F3.imprint","INTERSECT",VERTEX,{"derivedFrom":[subQ1,subQ0]});Q2=makeQuery(id+"F3.imprint","IMPRINT",FACE,{"disambiguationData":[TD([[makeQuery(id+"F3.imprint","IMPRINT",EDGE,{"disambiguationData":[TD([[subQ2,-1.0]])],"derivedFrom":subQ1}),1.0]])]});}
            var Q3;
            {var subQ0=sQuery(id+"F3.wireOp",EDGE,"E0.left");var subQ1=sQuery(id+"F3.wireOp",EDGE,"E0.bottom");var subQ2=makeQuery(id+"F3.imprint","INTERSECT",VERTEX,{"derivedFrom":[subQ1,subQ0]});Q3=makeQuery(id+"F3.imprint","IMPRINT",FACE,{"disambiguationData":[TD([[makeQuery(id+"F3.imprint","IMPRINT",EDGE,{"disambiguationData":[TD([[subQ2,-1.0]])],"derivedFrom":subQ1}),-1.0]])]});}
            var Q4;
            {var subQ0=sQuery(id+"F3.wireOp",EDGE,"E0.left");var subQ1=sQuery(id+"F3.wireOp",EDGE,"E0.top");var subQ2=makeQuery(id+"F3.imprint","INTERSECT",VERTEX,{"derivedFrom":[subQ1,subQ0]});Q4=makeQuery(id+"F3.imprint","IMPRINT",FACE,{"disambiguationData":[TD([[makeQuery(id+"F3.imprint","IMPRINT",EDGE,{"disambiguationData":[TD([[subQ2,-1.0]])],"derivedFrom":subQ1}),1.0]])]});}
            var Q5;
            {var subQ0=sQuery(id+"F3.wireOp",EDGE,"E0.left");var subQ1=sQuery(id+"F3.wireOp",EDGE,"E0.top");var subQ2=makeQuery(id+"F3.imprint","INTERSECT",VERTEX,{"derivedFrom":[subQ1,subQ0]});Q5=makeQuery(id+"F3.imprint","IMPRINT",FACE,{"disambiguationData":[TD([[makeQuery(id+"F3.imprint","IMPRINT",EDGE,{"disambiguationData":[TD([[subQ2,-1.0]])],"derivedFrom":subQ1}),-1.0]])]});}
            var Q6;
            {var subQ0=sQuery(id+"F3.wireOp",EDGE,"E0.right");var subQ1=sQuery(id+"F3.wireOp",EDGE,"E0.top");var subQ2=makeQuery(id+"F3.imprint","INTERSECT",VERTEX,{"derivedFrom":[subQ1,subQ0]});Q6=makeQuery(id+"F3.imprint","IMPRINT",FACE,{"disambiguationData":[TD([[makeQuery(id+"F3.imprint","IMPRINT",EDGE,{"disambiguationData":[TD([[subQ2,1.0]])],"derivedFrom":subQ1}),1.0]])]});}
            var Q7;
            {var subQ0=sQuery(id+"F3.wireOp",EDGE,"E0.right");var subQ1=sQuery(id+"F3.wireOp",EDGE,"E0.top");var subQ2=makeQuery(id+"F3.imprint","INTERSECT",VERTEX,{"derivedFrom":[subQ1,subQ0]});Q7=makeQuery(id+"F3.imprint","IMPRINT",FACE,{"disambiguationData":[TD([[makeQuery(id+"F3.imprint","IMPRINT",EDGE,{"disambiguationData":[TD([[subQ2,1.0]])],"derivedFrom":subQ1}),-1.0]])]});}
            extrude(context, id + "F10", {"entities" : qUnion([Q0, Q1, Q2, Q3, Q4, Q5, Q6, Q7]), "operationType" : NewBodyOperationType.REMOVE, "oppositeDirection" : true, "depth" : 25 * mm, "hasSecondDirection" : true, "secondDirectionOppositeDirection" : false, "secondDirectionDepth" : 25 * mm});
        }
        {
            var Q0;
            Q0=makeQuery(id+"F6.opExtrude","SWEPT_EDGE",EDGE,{"disambiguationData":[OSD([sQuery(id+"F4.wireOp",EDGE,"E22.0"),sQuery(id+"F4.wireOp",EDGE,"E28.3"),sQuery(id+"F4.wireOp",EDGE,"E34")])]});
            var Q1;
            Q1=makeQuery(id+"F6.opExtrude","SWEPT_EDGE",EDGE,{"disambiguationData":[OSD([sQuery(id+"F4.wireOp",EDGE,"E22.0"),sQuery(id+"F4.wireOp",EDGE,"E28.0"),sQuery(id+"F4.wireOp",EDGE,"E33")])]});
            var Q2;
            Q2=makeQuery(id+"F7.opExtrude","SWEPT_EDGE",EDGE,{"disambiguationData":[OSD([sQuery(id+"F4.wireOp",EDGE,"E22.0"),sQuery(id+"F4.wireOp",EDGE,"E28.0"),sQuery(id+"F4.wireOp",EDGE,"E33")])]});
            var Q3;
            Q3=makeQuery(id+"F7.opExtrude","SWEPT_EDGE",EDGE,{"disambiguationData":[OSD([sQuery(id+"F4.wireOp",EDGE,"E22.0"),sQuery(id+"F4.wireOp",EDGE,"E28.3"),sQuery(id+"F4.wireOp",EDGE,"E34")])]});
            fillet(context, id + "F11", {"entities" : qUnion([Q0, Q1, Q2, Q3]), "radius" : 1.5 * mm, "tangentPropagation" : true, "allowEdgeOverflow" : false});
        }
        {
            var Q0;
            Q0=makeQuery(id+"F6.opExtrude","SWEPT_EDGE",EDGE,{"disambiguationData":[OSD([sQuery(id+"F4.wireOp",EDGE,"E28.1"),sQuery(id+"F4.wireOp",EDGE,"E31")])]});
            var Q1;
            Q1=makeQuery(id+"F6.opExtrude","SWEPT_EDGE",EDGE,{"disambiguationData":[OSD([sQuery(id+"F4.wireOp",EDGE,"E28.2"),sQuery(id+"F4.wireOp",EDGE,"E32")])]});
            var Q2;
            Q2=makeQuery(id+"F7.opExtrude","SWEPT_EDGE",EDGE,{"disambiguationData":[OSD([sQuery(id+"F4.wireOp",EDGE,"E28.2"),sQuery(id+"F4.wireOp",EDGE,"E32")])]});
            var Q3;
            Q3=makeQuery(id+"F7.opExtrude","SWEPT_EDGE",EDGE,{"disambiguationData":[OSD([sQuery(id+"F4.wireOp",EDGE,"E28.1"),sQuery(id+"F4.wireOp",EDGE,"E31")])]});
            fillet(context, id + "F12", {"entities" : qUnion([Q0, Q1, Q2, Q3]), "radius" : 20 * mm, "tangentPropagation" : true, "allowEdgeOverflow" : false});
        }
        {
            var Q0;
            Q0=makeQuery(id+"F5.opExtrude","CAP_EDGE",EDGE,{"disambiguationData":[OSD([sQuery(id+"F3.wireOp",EDGE,"E2.4")])],"isStart":false});
            var Q1;
            Q1=makeQuery(id+"F5.opExtrude","CAP_EDGE",EDGE,{"disambiguationData":[OSD([sQuery(id+"F3.wireOp",EDGE,"E2.5")])],"isStart":false});
            var Q2;
            Q2=makeQuery(id+"F5.opExtrude","CAP_EDGE",EDGE,{"disambiguationData":[OSD([sQuery(id+"F3.wireOp",EDGE,"E2.6")])],"isStart":false});
            var Q3;
            Q3=makeQuery(id+"F5.opExtrude","CAP_EDGE",EDGE,{"disambiguationData":[OSD([sQuery(id+"F3.wireOp",EDGE,"E2.7")])],"isStart":false});
            var Q4;
            Q4=makeQuery(id+"F5.opExtrude","CAP_EDGE",EDGE,{"disambiguationData":[OSD([sQuery(id+"F3.wireOp",EDGE,"E2.3")])],"isStart":false});
            var Q5;
            Q5=makeQuery(id+"F5.opExtrude","CAP_EDGE",EDGE,{"disambiguationData":[OSD([sQuery(id+"F3.wireOp",EDGE,"E2.2")])],"isStart":false});
            var Q6;
            Q6=makeQuery(id+"F5.opExtrude","CAP_EDGE",EDGE,{"disambiguationData":[OSD([sQuery(id+"F3.wireOp",EDGE,"E3.5")])],"isStart":false});
            var Q7;
            Q7=makeQuery(id+"F5.opExtrude","CAP_EDGE",EDGE,{"disambiguationData":[OSD([sQuery(id+"F3.wireOp",EDGE,"E3.6")])],"isStart":false});
            var Q8;
            Q8=makeQuery(id+"F5.opExtrude","CAP_EDGE",EDGE,{"disambiguationData":[OSD([sQuery(id+"F3.wireOp",EDGE,"E3.4")])],"isStart":false});
            var Q9;
            Q9=makeQuery(id+"F5.opExtrude","CAP_EDGE",EDGE,{"disambiguationData":[OSD([sQuery(id+"F3.wireOp",EDGE,"E3.3")])],"isStart":false});
            var Q10;
            Q10=makeQuery(id+"F5.opExtrude","CAP_EDGE",EDGE,{"disambiguationData":[OSD([sQuery(id+"F3.wireOp",EDGE,"E3.1")])],"isStart":false});
            var Q11;
            Q11=makeQuery(id+"F5.opExtrude","CAP_EDGE",EDGE,{"disambiguationData":[OSD([sQuery(id+"F3.wireOp",EDGE,"E3.2")])],"isStart":false});
            var Q12;
            Q12=makeQuery(id+"F5.opExtrude","CAP_EDGE",EDGE,{"disambiguationData":[OSD([sQuery(id+"F3.wireOp",EDGE,"E1.0")])],"isStart":false});
            var Q13;
            Q13=makeQuery(id+"F5.opExtrude","CAP_EDGE",EDGE,{"disambiguationData":[OSD([sQuery(id+"F3.wireOp",EDGE,"E1.7")])],"isStart":false});
            var Q14;
            Q14=makeQuery(id+"F5.opExtrude","CAP_EDGE",EDGE,{"disambiguationData":[OSD([sQuery(id+"F3.wireOp",EDGE,"E1.6")])],"isStart":false});
            var Q15;
            Q15=makeQuery(id+"F5.opExtrude","CAP_EDGE",EDGE,{"disambiguationData":[OSD([sQuery(id+"F3.wireOp",EDGE,"E1.5")])],"isStart":false});
            var Q16;
            Q16=makeQuery(id+"F5.opExtrude","CAP_EDGE",EDGE,{"disambiguationData":[OSD([sQuery(id+"F3.wireOp",EDGE,"E1.4")])],"isStart":false});
            var Q17;
            Q17=makeQuery(id+"F5.opExtrude","CAP_EDGE",EDGE,{"disambiguationData":[OSD([sQuery(id+"F3.wireOp",EDGE,"E1.3")])],"isStart":false});
            var Q18;
            Q18=makeQuery(id+"F5.opExtrude","CAP_EDGE",EDGE,{"disambiguationData":[OSD([sQuery(id+"F3.wireOp",EDGE,"E4.7")])],"isStart":false});
            var Q19;
            Q19=makeQuery(id+"F5.opExtrude","CAP_EDGE",EDGE,{"disambiguationData":[OSD([sQuery(id+"F3.wireOp",EDGE,"E4.6")])],"isStart":false});
            var Q20;
            Q20=makeQuery(id+"F5.opExtrude","CAP_EDGE",EDGE,{"disambiguationData":[OSD([sQuery(id+"F3.wireOp",EDGE,"E4.5")])],"isStart":false});
            var Q21;
            Q21=makeQuery(id+"F5.opExtrude","CAP_EDGE",EDGE,{"disambiguationData":[OSD([sQuery(id+"F3.wireOp",EDGE,"E4.4")])],"isStart":false});
            var Q22;
            Q22=makeQuery(id+"F5.opExtrude","CAP_EDGE",EDGE,{"disambiguationData":[OSD([sQuery(id+"F3.wireOp",EDGE,"E4.3")])],"isStart":false});
            var Q23;
            Q23=makeQuery(id+"F5.opExtrude","CAP_EDGE",EDGE,{"disambiguationData":[OSD([sQuery(id+"F3.wireOp",EDGE,"E4.2")])],"isStart":false});
            fillet(context, id + "F13", {"entities" : qUnion([Q0, Q1, Q2, Q3, Q4, Q5, Q6, Q7, Q8, Q9, Q10, Q11, Q12, Q13, Q14, Q15, Q16, Q17, Q18, Q19, Q20, Q21, Q22, Q23]), "radius" : 2 * mm, "tangentPropagation" : true, "allowEdgeOverflow" : false});
        }
        {
            var Q0;
            Q0=makeQuery(id+"F7.opExtrude","CAP_EDGE",EDGE,{"disambiguationData":[OSD([sQuery(id+"F4.wireOp",EDGE,"E27")])],"isStart":false});
            var Q1;
            Q1=makeQuery(id+"F7.opExtrude","CAP_EDGE",EDGE,{"disambiguationData":[OSD([sQuery(id+"F4.wireOp",EDGE,"E26")])],"isStart":false});
            var Q2;
            Q2=makeQuery(id+"F6.opExtrude","CAP_EDGE",EDGE,{"disambiguationData":[OSD([sQuery(id+"F4.wireOp",EDGE,"E26")])],"isStart":false});
            var Q3;
            Q3=makeQuery(id+"F6.opExtrude","CAP_EDGE",EDGE,{"disambiguationData":[OSD([sQuery(id+"F4.wireOp",EDGE,"E27")])],"isStart":false});
            fillet(context, id + "F14", {"entities" : qUnion([Q0, Q1, Q2, Q3]), "radius" : 3 * mm, "tangentPropagation" : true, "allowEdgeOverflow" : false});
        }
        {
            var Q0;
            {var subQ0=sQuery(id+"F4.wireOp",EDGE,"E22.0");Q0=makeQuery(id+"F6.opExtrude","CAP_EDGE",EDGE,{"disambiguationData":[OSD([subQ0]),TDD([makeQuery(id+"F4.imprint","IMPRINT",EDGE,{"disambiguationData":[TD([[makeQuery(id+"F4.imprint","INTERSECT",VERTEX,{"derivedFrom":[subQ0,sQuery(id+"F4.wireOp",EDGE,"E26")]}),-1.0]])],"derivedFrom":subQ0})])],"isStart":false});}
            var Q1;
            {var subQ0=sQuery(id+"F4.wireOp",EDGE,"E22.0");Q1=makeQuery(id+"F7.opExtrude","CAP_EDGE",EDGE,{"disambiguationData":[OSD([subQ0]),TDD([makeQuery(id+"F4.imprint","IMPRINT",EDGE,{"disambiguationData":[TD([[makeQuery(id+"F4.imprint","INTERSECT",VERTEX,{"derivedFrom":[subQ0,sQuery(id+"F4.wireOp",EDGE,"E26")]}),-1.0]])],"derivedFrom":subQ0})])],"isStart":false});}
            fillet(context, id + "F15", {"entities" : qUnion([Q0, Q1]), "radius" : 3 * mm, "tangentPropagation" : true, "allowEdgeOverflow" : false});
        }
        {
            var Q0;
            Q0=makeQuery(id+"F4.imprint","IMPRINT",FACE,{"disambiguationData":[TD([[makeQuery(id+"F4.imprint","IMPRINT",EDGE,{"derivedFrom":sQuery(id+"F4.wireOp",EDGE,"E21")}),1.0]])]});
            extrude(context, id + "F16", {"entities" : qUnion([Q0]), "operationType" : NewBodyOperationType.REMOVE, "depth" : 25 * mm});
        }
        {
            var Q0;
            {var subQ0=sQuery(id+"F3.wireOp",EDGE,"E6");Q0=makeQuery(id+"F5.opExtrude","CAP_EDGE",EDGE,{"disambiguationData":[OSD([subQ0]),TDD([makeQuery(id+"F3.imprint","IMPRINT",EDGE,{"disambiguationData":[TD([[makeQuery(id+"F3.imprint","INTERSECT",VERTEX,{"derivedFrom":[subQ0,sQuery(id+"F3.wireOp",EDGE,"E7")]}),-1.0]])],"derivedFrom":subQ0})])],"isStart":false});}
            var Q1;
            {var subQ0=sQuery(id+"F3.wireOp",EDGE,"E5");Q1=makeQuery(id+"F5.opExtrude","CAP_EDGE",EDGE,{"disambiguationData":[OSD([subQ0]),TDD([makeQuery(id+"F3.imprint","IMPRINT",EDGE,{"disambiguationData":[TD([[makeQuery(id+"F3.imprint","INTERSECT",VERTEX,{"disambiguationData":[OD(0.0)],"derivedFrom":[subQ0,sQuery(id+"F3.wireOp",EDGE,"E13")]}),1.0]])],"derivedFrom":subQ0})])],"isStart":false});}
            var Q2;
            {var subQ0=sQuery(id+"F3.wireOp",EDGE,"E7");Q2=makeQuery(id+"F5.opExtrude","CAP_EDGE",EDGE,{"disambiguationData":[OSD([subQ0]),TDD([makeQuery(id+"F3.imprint","IMPRINT",EDGE,{"disambiguationData":[TD([[makeQuery(id+"F3.imprint","INTERSECT",VERTEX,{"derivedFrom":[sQuery(id+"F3.wireOp",EDGE,"E6"),subQ0]}),1.0]])],"derivedFrom":subQ0})])],"isStart":false});}
            var Q3;
            {var subQ0=sQuery(id+"F3.wireOp",EDGE,"E8");Q3=makeQuery(id+"F5.opExtrude","CAP_EDGE",EDGE,{"disambiguationData":[OSD([subQ0]),TDD([makeQuery(id+"F3.imprint","IMPRINT",EDGE,{"disambiguationData":[TD([[makeQuery(id+"F3.imprint","INTERSECT",VERTEX,{"disambiguationData":[OD(1.0)],"derivedFrom":[subQ0,sQuery(id+"F3.wireOp",EDGE,"E13")]}),-1.0]])],"derivedFrom":subQ0})])],"isStart":false});}
            var Q4;
            {var subQ0=sQuery(id+"F3.wireOp",EDGE,"E6");Q4=makeQuery(id+"F5.opExtrude","CAP_EDGE",EDGE,{"disambiguationData":[OSD([subQ0]),TDD([makeQuery(id+"F3.imprint","IMPRINT",EDGE,{"disambiguationData":[TD([[makeQuery(id+"F3.imprint","INTERSECT",VERTEX,{"disambiguationData":[OD(0.0)],"derivedFrom":[subQ0,sQuery(id+"F3.wireOp",EDGE,"E13")]}),1.0]])],"derivedFrom":subQ0})])],"isStart":false});}
            var Q5;
            {var subQ0=sQuery(id+"F3.wireOp",EDGE,"E5");Q5=makeQuery(id+"F5.opExtrude","CAP_EDGE",EDGE,{"disambiguationData":[OSD([subQ0]),TDD([makeQuery(id+"F3.imprint","IMPRINT",EDGE,{"disambiguationData":[TD([[makeQuery(id+"F3.imprint","INTERSECT",VERTEX,{"derivedFrom":[subQ0,sQuery(id+"F3.wireOp",EDGE,"E8")]}),-1.0]])],"derivedFrom":subQ0})])],"isStart":false});}
            var Q6;
            {var subQ0=sQuery(id+"F3.wireOp",EDGE,"E8");Q6=makeQuery(id+"F5.opExtrude","CAP_EDGE",EDGE,{"disambiguationData":[OSD([subQ0]),TDD([makeQuery(id+"F3.imprint","IMPRINT",EDGE,{"disambiguationData":[TD([[makeQuery(id+"F3.imprint","INTERSECT",VERTEX,{"derivedFrom":[sQuery(id+"F3.wireOp",EDGE,"E5"),subQ0]}),1.0]])],"derivedFrom":subQ0})])],"isStart":false});}
            var Q7;
            {var subQ0=sQuery(id+"F3.wireOp",EDGE,"E7");Q7=makeQuery(id+"F5.opExtrude","CAP_EDGE",EDGE,{"disambiguationData":[OSD([subQ0]),TDD([makeQuery(id+"F3.imprint","IMPRINT",EDGE,{"disambiguationData":[TD([[makeQuery(id+"F3.imprint","INTERSECT",VERTEX,{"disambiguationData":[OD(1.0)],"derivedFrom":[subQ0,sQuery(id+"F3.wireOp",EDGE,"E13")]}),-1.0]])],"derivedFrom":subQ0})])],"isStart":false});}
            chamfer(context, id + "F17", {"entities" : qUnion([Q0, Q1, Q2, Q3, Q4, Q5, Q6, Q7]), "width" : 1.5 * mm, "tangentPropagation" : true});
        }
        {
            var Q0;
            Q0=makeQuery(id+"F4.imprint","IMPRINT",FACE,{"disambiguationData":[TD([[makeQuery(id+"F4.imprint","IMPRINT",EDGE,{"derivedFrom":sQuery(id+"F4.wireOp",EDGE,"E21")}),1.0]])]});
            extrude(context, id + "F18", {"entities" : qUnion([Q0]), "depth" : (getVariable(context, 'bucket_width') / 2 + getVariable(context, 'shell') * 3) * mm, "hasSecondDirection" : true, "secondDirectionOppositeDirection" : true, "secondDirectionDepth" : (getVariable(context, 'bucket_width') / 2 + getVariable(context, 'shell')) * mm});
        }
        {
            var Q0;
            Q0=makeQuery(id+"F4.imprint","IMPRINT",FACE,{"disambiguationData":[TD([[makeQuery(id+"F4.imprint","IMPRINT",EDGE,{"derivedFrom":sQuery(id+"F4.wireOp",EDGE,"E21")}),-1.0]])]});
            extrude(context, id + "F19", {"entities" : qUnion([Q0]), "depth" : (getVariable(context, 'bucket_width') / 2 - getVariable(context, 'shell')) * mm, "hasSecondDirection" : true, "secondDirectionOppositeDirection" : false, "secondDirectionDepth" : (getVariable(context, 'bearing_width') / 2 + 1) * mm});
        }
        {
            var Q0;
            Q0=makeQuery(id+"F4.imprint","IMPRINT",FACE,{"disambiguationData":[TD([[makeQuery(id+"F4.imprint","IMPRINT",EDGE,{"derivedFrom":sQuery(id+"F4.wireOp",EDGE,"E21")}),-1.0]])]});
            extrude(context, id + "F20", {"entities" : qUnion([Q0]), "oppositeDirection" : true, "depth" : (getVariable(context, 'bucket_width') / 2 - getVariable(context, 'shell')) * mm, "hasSecondDirection" : true, "secondDirectionOppositeDirection" : true, "secondDirectionDepth" : (getVariable(context, 'bearing_width') / 2 + 1) * mm});
        }
        {
            var Q0;
            Q0=makeQuery(id+"F6.opExtrude","CAP_EDGE",EDGE,{"disambiguationData":[OSD([sQuery(id+"F4.wireOp",EDGE,"E34")])],"isStart":false});
            var Q1;
            Q1=makeQuery(id+"F6.opExtrude","CAP_EDGE",EDGE,{"disambiguationData":[OSD([sQuery(id+"F4.wireOp",EDGE,"E32")])],"isStart":false});
            var Q2;
            {var subQ0=sQuery(id+"F4.wireOp",EDGE,"E31");var subQ1=sQuery(id+"F4.wireOp",EDGE,"E28.1");Q2=makeQuery(id+"F12.opFillet","BLEND_EDGE",EDGE,{"blendedFrom":[makeQuery(id+"F6.opExtrude","SWEPT_EDGE",EDGE,{"disambiguationData":[OSD([subQ1,subQ0])]}),makeQuery(id+"F6.opExtrude","CAP_FACE",FACE,{"disambiguationData":[OSD([sQuery(id+"F4.wireOp",EDGE,"E22.0"),sQuery(id+"F4.wireOp",EDGE,"E23"),sQuery(id+"F4.wireOp",EDGE,"E24"),sQuery(id+"F4.wireOp",EDGE,"E26"),sQuery(id+"F4.wireOp",EDGE,"E27"),sQuery(id+"F4.wireOp",EDGE,"E28.0"),subQ1,sQuery(id+"F4.wireOp",EDGE,"E28.2"),sQuery(id+"F4.wireOp",EDGE,"E28.3"),subQ0,sQuery(id+"F4.wireOp",EDGE,"E32"),sQuery(id+"F4.wireOp",EDGE,"E33"),sQuery(id+"F4.wireOp",EDGE,"E34")])],"isStart":false})],"blendedInto":[makeQuery(id+"F6.opExtrude","CAP_FACE",FACE,{"disambiguationData":[OSD([sQuery(id+"F4.wireOp",EDGE,"E22.0"),sQuery(id+"F4.wireOp",EDGE,"E23"),sQuery(id+"F4.wireOp",EDGE,"E24"),sQuery(id+"F4.wireOp",EDGE,"E26"),sQuery(id+"F4.wireOp",EDGE,"E27"),sQuery(id+"F4.wireOp",EDGE,"E28.0"),subQ1,sQuery(id+"F4.wireOp",EDGE,"E28.2"),sQuery(id+"F4.wireOp",EDGE,"E28.3"),subQ0,sQuery(id+"F4.wireOp",EDGE,"E32"),sQuery(id+"F4.wireOp",EDGE,"E33"),sQuery(id+"F4.wireOp",EDGE,"E34")])],"isStart":false})]});}
            var Q3;
            {var subQ0=sQuery(id+"F4.wireOp",EDGE,"E32");var subQ1=sQuery(id+"F4.wireOp",EDGE,"E28.2");Q3=makeQuery(id+"F12.opFillet","BLEND_EDGE",EDGE,{"blendedFrom":[makeQuery(id+"F7.opExtrude","SWEPT_EDGE",EDGE,{"disambiguationData":[OSD([subQ1,subQ0])]}),makeQuery(id+"F7.opExtrude","CAP_FACE",FACE,{"disambiguationData":[OSD([sQuery(id+"F4.wireOp",EDGE,"E22.0"),sQuery(id+"F4.wireOp",EDGE,"E23"),sQuery(id+"F4.wireOp",EDGE,"E24"),sQuery(id+"F4.wireOp",EDGE,"E26"),sQuery(id+"F4.wireOp",EDGE,"E27"),sQuery(id+"F4.wireOp",EDGE,"E28.0"),sQuery(id+"F4.wireOp",EDGE,"E28.1"),subQ1,sQuery(id+"F4.wireOp",EDGE,"E28.3"),sQuery(id+"F4.wireOp",EDGE,"E31"),subQ0,sQuery(id+"F4.wireOp",EDGE,"E33"),sQuery(id+"F4.wireOp",EDGE,"E34")])],"isStart":false})],"blendedInto":[makeQuery(id+"F7.opExtrude","CAP_FACE",FACE,{"disambiguationData":[OSD([sQuery(id+"F4.wireOp",EDGE,"E22.0"),sQuery(id+"F4.wireOp",EDGE,"E23"),sQuery(id+"F4.wireOp",EDGE,"E24"),sQuery(id+"F4.wireOp",EDGE,"E26"),sQuery(id+"F4.wireOp",EDGE,"E27"),sQuery(id+"F4.wireOp",EDGE,"E28.0"),sQuery(id+"F4.wireOp",EDGE,"E28.1"),subQ1,sQuery(id+"F4.wireOp",EDGE,"E28.3"),sQuery(id+"F4.wireOp",EDGE,"E31"),subQ0,sQuery(id+"F4.wireOp",EDGE,"E33"),sQuery(id+"F4.wireOp",EDGE,"E34")])],"isStart":false})]});}
            var Q4;
            {var subQ0=sQuery(id+"F4.wireOp",EDGE,"E31");var subQ1=sQuery(id+"F4.wireOp",EDGE,"E28.1");Q4=makeQuery(id+"F12.opFillet","BLEND_EDGE",EDGE,{"blendedFrom":[makeQuery(id+"F7.opExtrude","SWEPT_EDGE",EDGE,{"disambiguationData":[OSD([subQ1,subQ0])]}),makeQuery(id+"F7.opExtrude","CAP_FACE",FACE,{"disambiguationData":[OSD([sQuery(id+"F4.wireOp",EDGE,"E22.0"),sQuery(id+"F4.wireOp",EDGE,"E23"),sQuery(id+"F4.wireOp",EDGE,"E24"),sQuery(id+"F4.wireOp",EDGE,"E26"),sQuery(id+"F4.wireOp",EDGE,"E27"),sQuery(id+"F4.wireOp",EDGE,"E28.0"),subQ1,sQuery(id+"F4.wireOp",EDGE,"E28.2"),sQuery(id+"F4.wireOp",EDGE,"E28.3"),subQ0,sQuery(id+"F4.wireOp",EDGE,"E32"),sQuery(id+"F4.wireOp",EDGE,"E33"),sQuery(id+"F4.wireOp",EDGE,"E34")])],"isStart":false})],"blendedInto":[makeQuery(id+"F7.opExtrude","CAP_FACE",FACE,{"disambiguationData":[OSD([sQuery(id+"F4.wireOp",EDGE,"E22.0"),sQuery(id+"F4.wireOp",EDGE,"E23"),sQuery(id+"F4.wireOp",EDGE,"E24"),sQuery(id+"F4.wireOp",EDGE,"E26"),sQuery(id+"F4.wireOp",EDGE,"E27"),sQuery(id+"F4.wireOp",EDGE,"E28.0"),subQ1,sQuery(id+"F4.wireOp",EDGE,"E28.2"),sQuery(id+"F4.wireOp",EDGE,"E28.3"),subQ0,sQuery(id+"F4.wireOp",EDGE,"E32"),sQuery(id+"F4.wireOp",EDGE,"E33"),sQuery(id+"F4.wireOp",EDGE,"E34")])],"isStart":false})]});}
            var Q5;
            Q5=makeQuery(id+"F6.opExtrude","CAP_EDGE",EDGE,{"disambiguationData":[OSD([sQuery(id+"F4.wireOp",EDGE,"E28.0")])],"isStart":false});
            var Q6;
            Q6=makeQuery(id+"F7.opExtrude","CAP_EDGE",EDGE,{"disambiguationData":[OSD([sQuery(id+"F4.wireOp",EDGE,"E28.0")])],"isStart":false});
            var Q7;
            Q7=makeQuery(id+"F7.opExtrude","CAP_EDGE",EDGE,{"disambiguationData":[OSD([sQuery(id+"F4.wireOp",EDGE,"E28.3")])],"isStart":false});
            fillet(context, id + "F21", {"entities" : qUnion([Q0, Q1, Q2, Q3, Q4, Q5, Q6, Q7]), "radius" : 2 * mm, "tangentPropagation" : true, "allowEdgeOverflow" : false});
        }
        {
            var Q0;
            {var subQ0=sQuery(id+"F4.wireOp",EDGE,"E22.0");Q0=makeQuery(id+"F8.boolean.opBoolean","INTERSECT",EDGE,{"disambiguationData":[OD(2.0)],"derivedFrom":[makeQuery(id+"F6.opExtrude","CAP_FACE",FACE,{"disambiguationData":[OSD([sQuery(id+"F4.wireOp",EDGE,"E21"),subQ0,sQuery(id+"F4.wireOp",EDGE,"E23"),sQuery(id+"F4.wireOp",EDGE,"E24"),sQuery(id+"F4.wireOp",EDGE,"E26"),sQuery(id+"F4.wireOp",EDGE,"E27"),sQuery(id+"F4.wireOp",EDGE,"E28.0"),sQuery(id+"F4.wireOp",EDGE,"E28.1"),sQuery(id+"F4.wireOp",EDGE,"E28.2"),sQuery(id+"F4.wireOp",EDGE,"E28.3"),sQuery(id+"F4.wireOp",EDGE,"E31"),sQuery(id+"F4.wireOp",EDGE,"E32"),sQuery(id+"F4.wireOp",EDGE,"E33"),sQuery(id+"F4.wireOp",EDGE,"E34")])],"isStart":true}),makeQuery(id+"F8.opExtrude","SWEPT_FACE",FACE,{"disambiguationData":[OSD([subQ0])]})]});}
            var Q1;
            {var subQ0=sQuery(id+"F4.wireOp",EDGE,"E22.0");Q1=makeQuery(id+"F9.boolean.opBoolean","INTERSECT",EDGE,{"disambiguationData":[OD(2.0)],"derivedFrom":[makeQuery(id+"F7.opExtrude","CAP_FACE",FACE,{"disambiguationData":[OSD([subQ0,sQuery(id+"F4.wireOp",EDGE,"E23"),sQuery(id+"F4.wireOp",EDGE,"E24"),sQuery(id+"F4.wireOp",EDGE,"E26"),sQuery(id+"F4.wireOp",EDGE,"E27"),sQuery(id+"F4.wireOp",EDGE,"E28.0"),sQuery(id+"F4.wireOp",EDGE,"E28.1"),sQuery(id+"F4.wireOp",EDGE,"E28.2"),sQuery(id+"F4.wireOp",EDGE,"E28.3"),sQuery(id+"F4.wireOp",EDGE,"E31"),sQuery(id+"F4.wireOp",EDGE,"E32"),sQuery(id+"F4.wireOp",EDGE,"E33"),sQuery(id+"F4.wireOp",EDGE,"E34")])],"isStart":true}),makeQuery(id+"F9.opExtrude","SWEPT_FACE",FACE,{"disambiguationData":[OSD([subQ0])]})]});}
            fillet(context, id + "F22", {"entities" : qUnion([Q0, Q1]), "radius" : 5 * mm, "tangentPropagation" : true, "allowEdgeOverflow" : false});
        }
    });
